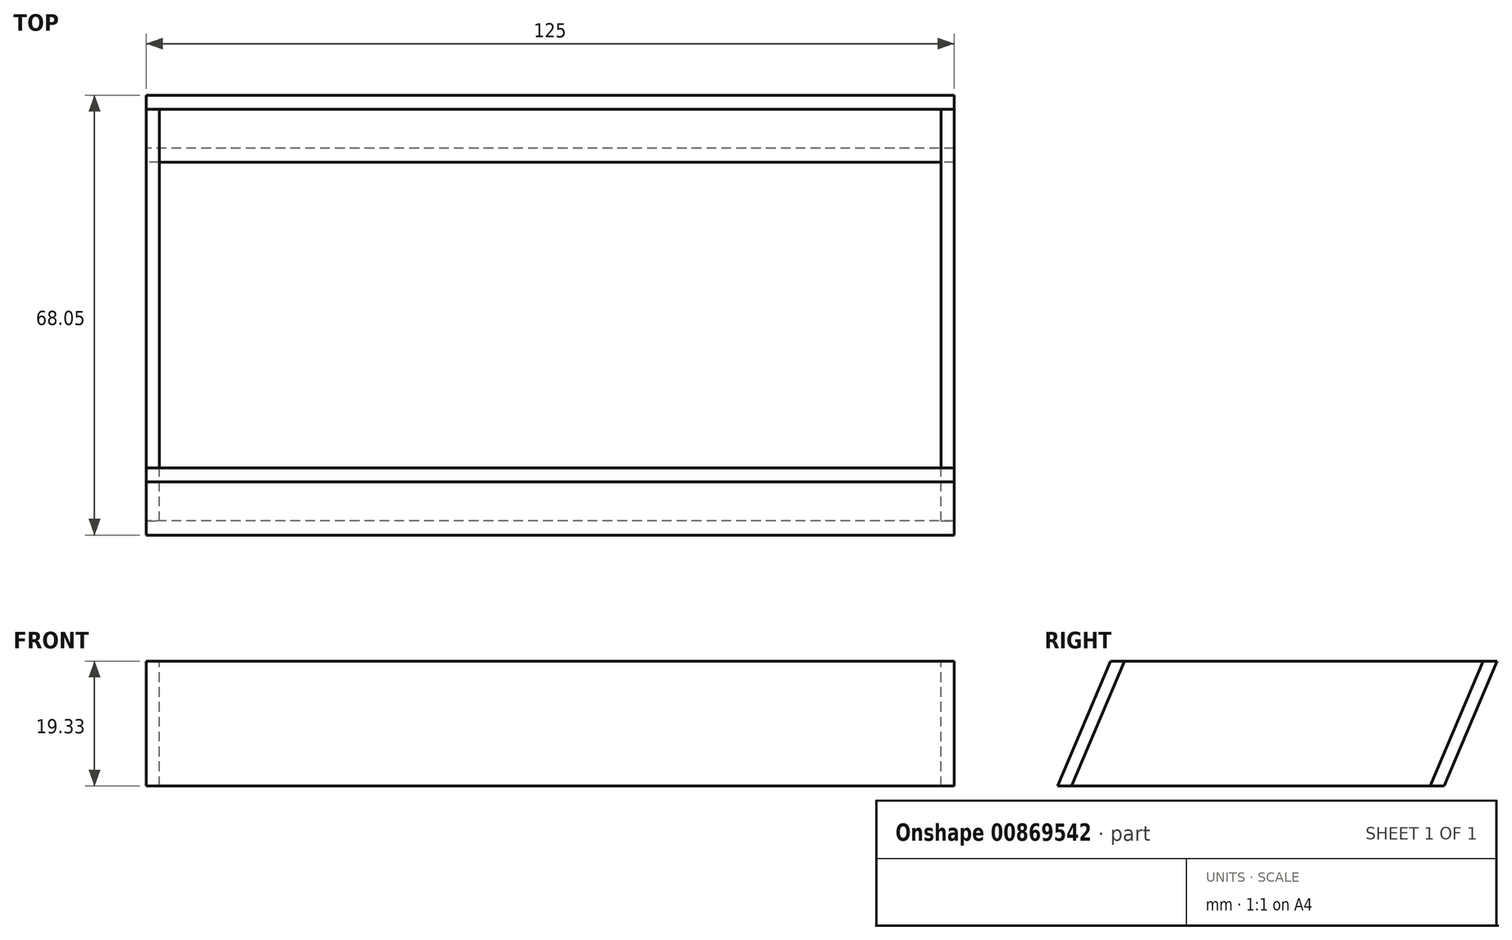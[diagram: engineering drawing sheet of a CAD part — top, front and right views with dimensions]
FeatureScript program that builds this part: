
annotation { "Feature Type Name" : "Feature", "Feature Type Description" : "" }
export const myFeature = defineFeature(function(context is Context, id is Id, definition is map)
    precondition{}
    {
        {
            var Q0;
            Q0=qCreatedBy(makeId("Right.planeOp"),FACE);
            var sketch = newSketch(context, id + "F0", { "sketchPlane" : qUnion([Q0])});
            skLineSegment(sketch, "E0", {"start": v(-23.6, 0) * mm, "end": v(36.24, 0) * mm});
            skLineSegment(sketch, "E1", {"start": v(36.24, 0) * mm, "end": v(28.04, -19.33) * mm});
            skLineSegment(sketch, "E2", {"start": v(-23.6, 0) * mm, "end": v(-31.8, -19.33) * mm});
            skLineSegment(sketch, "E3", {"start": v(-31.8, -19.33) * mm, "end": v(28.04, -19.33) * mm});
            skLineSegment(sketch, "E4", {"start": v(-29.64, -19.33) * mm, "end": v(-21.43, 0) * mm});
            skLineSegment(sketch, "E5", {"start": v(-21.43, 0) * mm, "end": v(-23.6, 0) * mm});
            skLineSegment(sketch, "E6", {"start": v(36.24, 0) * mm, "end": v(34.07, 0) * mm});
            skLineSegment(sketch, "E7", {"start": v(34.07, 0) * mm, "end": v(25.87, -19.33) * mm});
            skLineSegment(sketch, "E8", {"start": v(25.87, -19.33) * mm, "end": v(28.04, -19.33) * mm});
            skSolve(sketch);
        }
        {
            var Q0;
            {var subQ0=sQuery(id+"F0.wireOp",EDGE,"E4");Q0=makeQuery(id+"F0.imprint","IMPRINT",FACE,{"disambiguationData":[TD([[makeQuery(id+"F0.imprint","IMPRINT",EDGE,{"derivedFrom":subQ0}),-1.0]])]});}
            extrude(context, id + "F1", {"entities" : qUnion([Q0]), "oppositeDirection" : true, "depth" : 2 * mm, "offsetDistance" : 25 * mm});
        }
        {
            var Q0;
            {var subQ0=sQuery(id+"F0.wireOp",EDGE,"E1");Q0=makeQuery(id+"F0.imprint","IMPRINT",FACE,{"disambiguationData":[TD([[makeQuery(id+"F0.imprint","IMPRINT",EDGE,{"derivedFrom":subQ0}),-1.0]])]});}
            var Q1;
            {var subQ2=sQuery(id+"F0.wireOp",EDGE,"E2");Q1=makeQuery(id+"F0.imprint","IMPRINT",FACE,{"disambiguationData":[TD([[makeQuery(id+"F0.imprint","IMPRINT",EDGE,{"derivedFrom":subQ2}),1.0]])]});}
            extrude(context, id + "F2", {"entities" : qUnion([Q0, Q1]), "depth" : 123 * mm, "offsetDistance" : 25 * mm, "hasSecondDirection" : true, "secondDirectionOppositeDirection" : true, "secondDirectionDepth" : 2 * mm});
        }
        {
            var Q0;
            Q0=makeQuery(id+"F1.opExtrude","SWEPT_BODY",BODY,{"disambiguationData":[OSD([sQuery(id+"F0.wireOp",EDGE,"E0"),sQuery(id+"F0.wireOp",EDGE,"E3"),sQuery(id+"F0.wireOp",EDGE,"E4"),sQuery(id+"F0.wireOp",EDGE,"E7")])]});
            transform(context, id + "F3", {"entities" : qUnion([Q0]), "transformType" : TransformType.TRANSLATION_3D, "dx" : 123 * mm, "dy" : 0 * mm, "dz" : 0 * mm, "makeCopy" : true});
        }
    });
